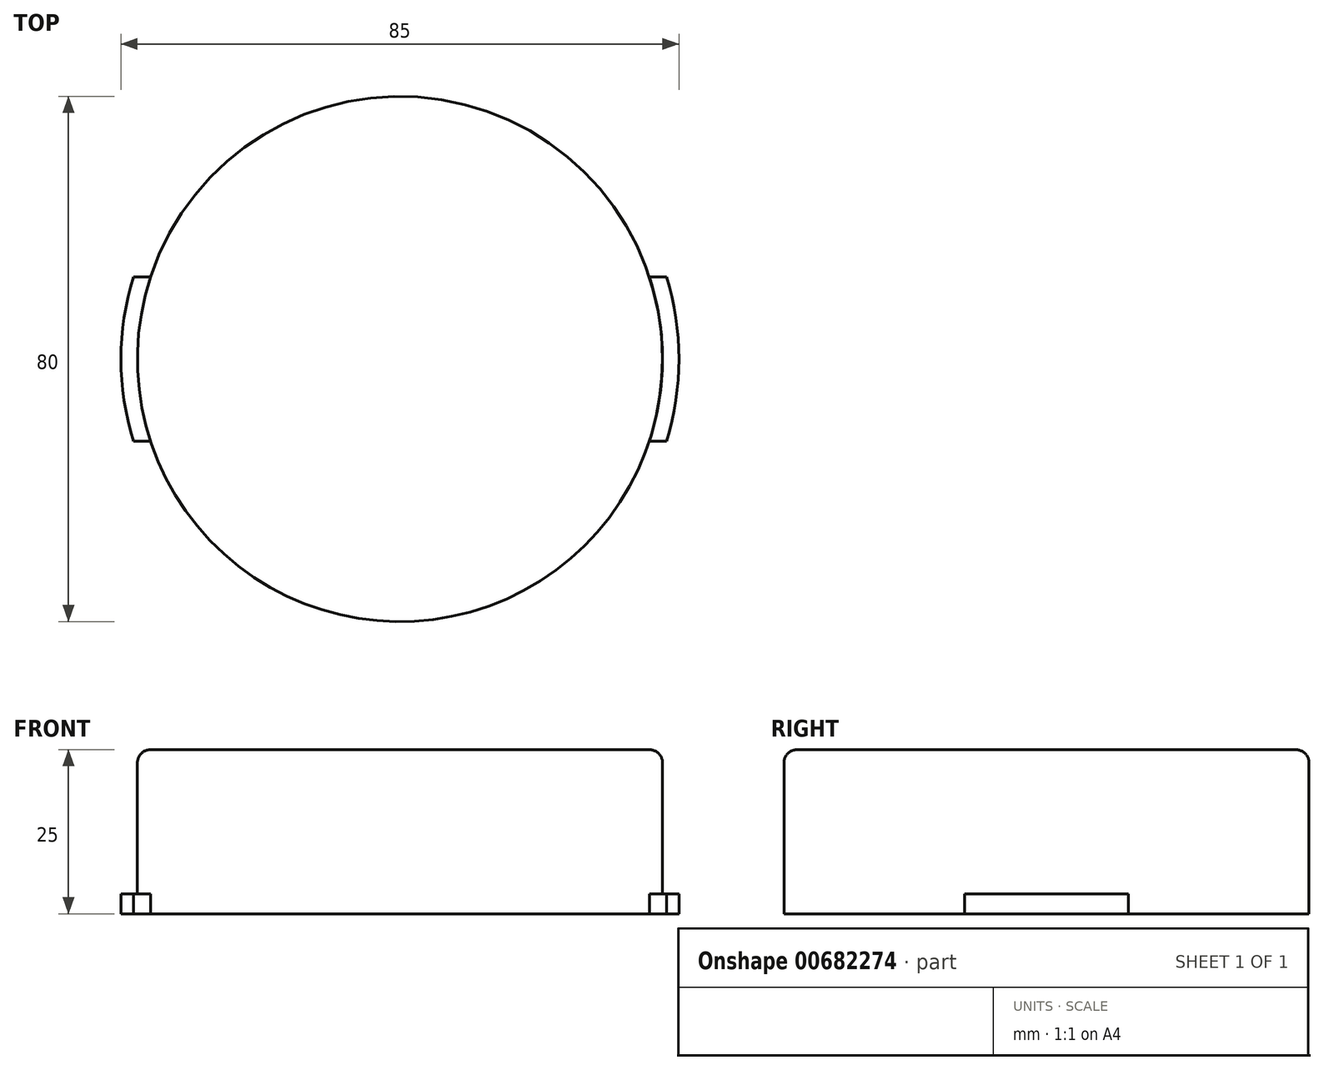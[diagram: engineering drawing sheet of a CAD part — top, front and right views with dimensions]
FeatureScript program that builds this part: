
annotation { "Feature Type Name" : "Feature", "Feature Type Description" : "" }
export const myFeature = defineFeature(function(context is Context, id is Id, definition is map)
    precondition{}
    {
        {
            var Q0;
            Q0=qCreatedBy(makeId("Top.planeOp"),FACE);
            var sketch = newSketch(context, id + "F0", { "sketchPlane" : qUnion([Q0])});
            skCircle(sketch, "E0", {"center": v(0, 0) * mm, "radius": 40 * mm});
            skSolve(sketch);
        }
        {
            var Q0;
            Q0=makeQuery(id+"F0.imprint","IMPRINT",FACE,{"disambiguationData":[TD([[makeQuery(id+"F0.imprint","IMPRINT",EDGE,{"derivedFrom":sQuery(id+"F0.wireOp",EDGE,"E0")}),1.0]])]});
            var sketch = newSketch(context, id + "F1", { "sketchPlane" : qUnion([Q0])});
            skSolve(sketch);
        }
        {
            var Q0;
            Q0=makeQuery(id+"F1.imprint","IMPRINT",FACE,{"disambiguationData":[TD([[makeQuery(id+"F1.imprint","IMPRINT",EDGE,{"derivedFrom":makeQuery(id+"F0.imprint","IMPRINT",EDGE,{"derivedFrom":sQuery(id+"F0.wireOp",EDGE,"E0")})}),1.0]])]});
            extrude(context, id + "F2", {"entities" : qUnion([Q0]), "depth" : 25 * mm, "offsetDistance" : 25 * mm});
        }
        {
            var Q0;
            Q0=makeQuery(id+"F0.imprint","IMPRINT",FACE,{"disambiguationData":[TD([[makeQuery(id+"F0.imprint","IMPRINT",EDGE,{"derivedFrom":sQuery(id+"F0.wireOp",EDGE,"E0")}),1.0]])]});
            var sketch = newSketch(context, id + "F3", { "sketchPlane" : qUnion([Q0])});
            skArc(sketch, "E1", {"start": v(40.62, -12.5) * mm, "mid": v(42.5, 0) * mm, "end": v(40.62, 12.5) * mm});
            skLineSegment(sketch, "E2", {"start": v(-40.62, -12.5) * mm, "end": v(40.62, -12.5) * mm});
            skLineSegment(sketch, "E3", {"start": v(-40.62, 12.5) * mm, "end": v(40.62, 12.5) * mm});
            skArc(sketch, "E4.trimOffspring", {"start": v(-40.62, 12.5) * mm, "mid": v(-42.5, 0) * mm, "end": v(-40.62, -12.5) * mm});
            skSolve(sketch);
        }
        {
            var Q0;
            Q0 = qSketchRegion(id + "F3", true);
            extrude(context, id + "F4", {"entities" : qUnion([Q0]), "operationType" : NewBodyOperationType.ADD, "depth" : 3 * mm, "offsetDistance" : 25 * mm});
        }
        {
            var Q0;
            Q0=makeQuery(id+"F2.opExtrude","CAP_EDGE",EDGE,{"disambiguationData":[OSD([sQuery(id+"F0.wireOp",EDGE,"E0")])],"isStart":false});
            fillet(context, id + "F5", {"entities" : qUnion([Q0]), "radius" : 2 * mm, "tangentPropagation" : true, "allowEdgeOverflow" : false});
        }
    });
